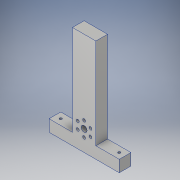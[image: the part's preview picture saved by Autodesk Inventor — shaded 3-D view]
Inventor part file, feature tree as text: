
AUTODESK INVENTOR PART (.ipt)
format: ipt  version: 2019 (Build 230136000, 136)  size: 152,064 bytes
history: native  units: in
note: dims shown in document units (in); Inventor stores cm internally (conversion verified against a paired STEP export)
features: sketch x5, hole x3, extrude x2, pattern_circular x1, plane x1, mirror x1, projected_geometry x1
ambient origin geometry x8: Origin, YZ Plane, XZ Plane, XY Plane, X Axis, Y Axis, Z Axis, Center Point
bodies: Solid1 (feature_tree)
feature tree (14):
  extrude  "Extrusion1"  Depth=4.375in
  hole  "Hole1"  [1 undecoded]
  hole  "Hole2"  [1 undecoded]
  pattern_circular  "Circular Pattern1"  [2 undecoded]
  extrude  "Extrusion2"  Depth=0.5in TaperAngle=360.0deg
  plane  "Work Plane1"
  mirror  "Mirror1"
  hole  "Hole3"  [1 undecoded]
  sketch  "Sketch1"  dims[d0=1.0in d1=4.375in]
  sketch  "Sketch2"  dims[d2=0.5in d3=0.0in d4=3.5in]
  sketch  "Sketch3"  dims[d5=1.0in d6=0.5in]
  sketch  "Sketch5"  dims[d7=0.25in d8=0.75in d9=0.375in d10=0.25in d11=0.5635in d12=1.0in d13=0.8108in]
  sketch  "Sketch7"  dims[d14=0.315in d15=0.5in d16=0.125in d17=0.75in d18=0.375in d19=0.25in d20=0.5635in d21=1.0in d22=0.8108in d23=2.3622in d24=360.0deg d26=0.5in d27=1.0in d28=0.0in d29=0.5in d30=0.25in d31=0.25in d32=0.25in d33=0.25in d34=0.104in d35=0.276in d36=0.375in d37=0.25in d38=0.5635in d39=0.432in d40=0.8108in]
  projected_geometry  "Projected Loop1"
note: 5 required parameter values undecoded (feature->parameter linkage not recoverable at this tier; creation-order binding heuristic only, values carry confidence <= 0.55)
